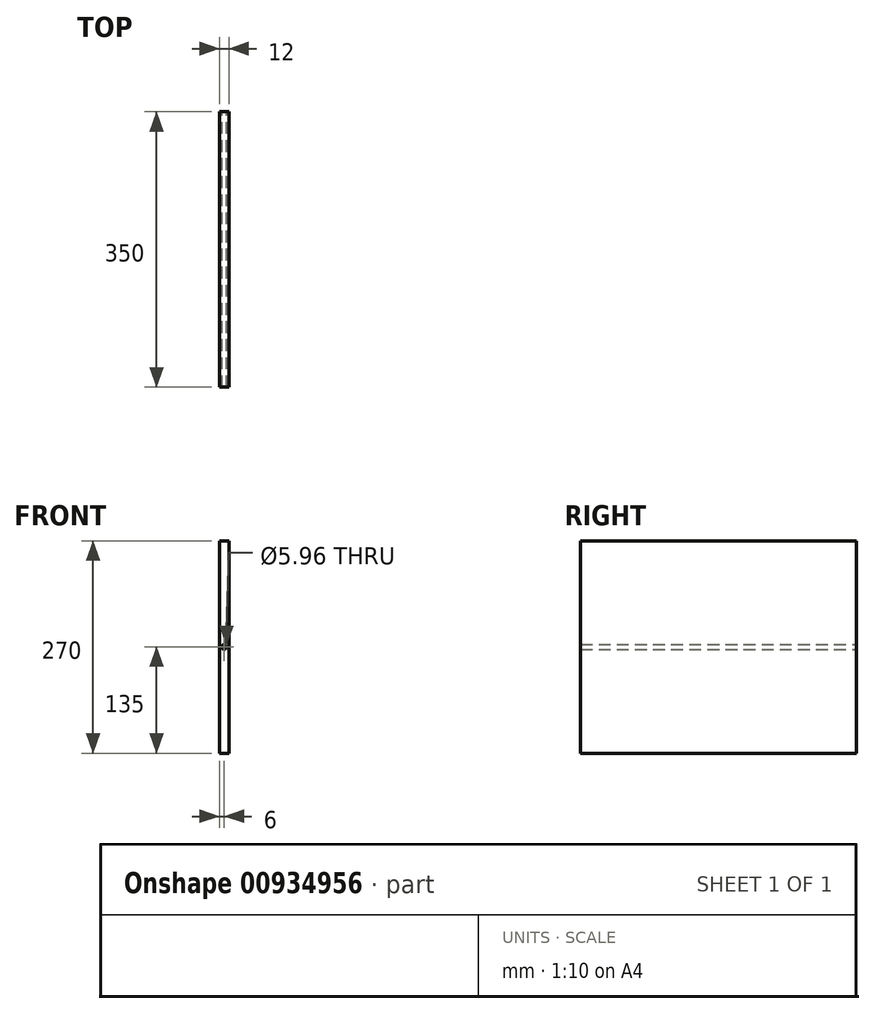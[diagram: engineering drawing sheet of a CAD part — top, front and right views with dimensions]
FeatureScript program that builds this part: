
annotation { "Feature Type Name" : "Feature", "Feature Type Description" : "" }
export const myFeature = defineFeature(function(context is Context, id is Id, definition is map)
    precondition{}
    {
        {
            var Q0;
            Q0=qCreatedBy(makeId("Front.planeOp"),FACE);
            var sketch = newSketch(context, id + "F0", { "sketchPlane" : qUnion([Q0])});
            skLineSegment(sketch, "E0.bottom", {"start": v(0, 0) * mm, "end": v(12, 0) * mm});
            skLineSegment(sketch, "E0.top", {"start": v(0, 270) * mm, "end": v(12, 270) * mm});
            skLineSegment(sketch, "E0.left", {"start": v(0, 0) * mm, "end": v(0, 270) * mm});
            skLineSegment(sketch, "E0.right", {"start": v(12, 0) * mm, "end": v(12, 270) * mm});
            skCircle(sketch, "E1", {"center": v(6, 135) * mm, "radius": 2.98 * mm});
            skPoint(sketch, "E2.orphan", {"position": v(12, 135) * mm});
            skPoint(sketch, "E3.start.orphan", {"position": v(0, 135) * mm});
            skSolve(sketch);
        }
        {
            var Q0;
            Q0 = qSketchRegion(id + "F0", true);
            extrude(context, id + "F1", {"entities" : qUnion([Q0]), "depth" : 350 * mm, "offsetDistance" : 25 * mm});
        }
    });
